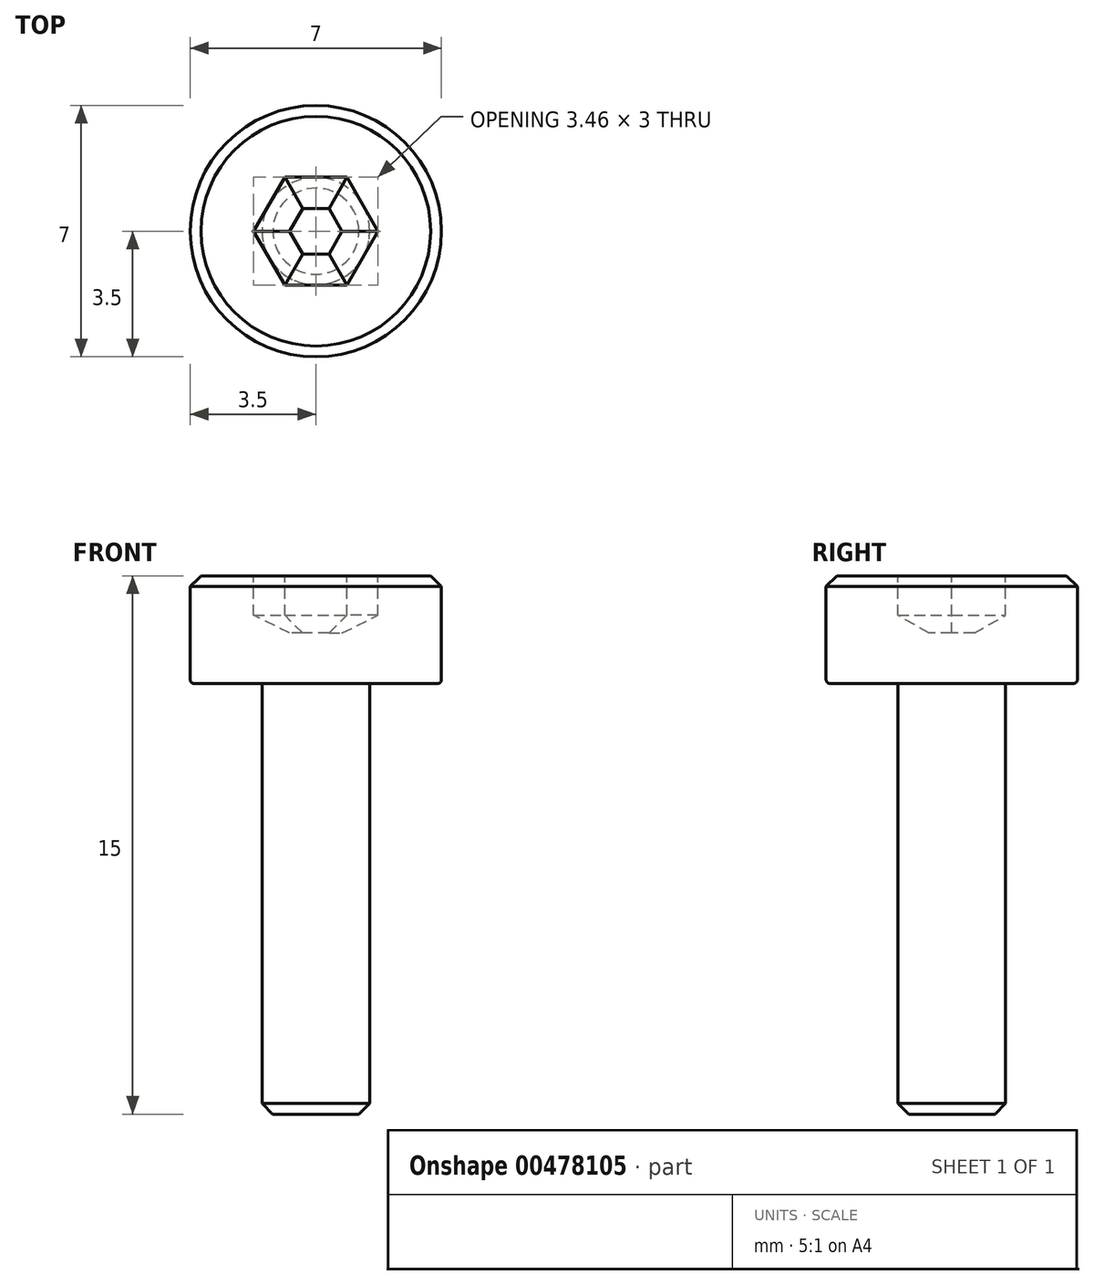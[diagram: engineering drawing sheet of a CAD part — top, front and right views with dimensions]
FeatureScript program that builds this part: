
annotation { "Feature Type Name" : "Feature", "Feature Type Description" : "" }
export const myFeature = defineFeature(function(context is Context, id is Id, definition is map)
    precondition{}
    {
        {
            var Q0;
            Q0=qCreatedBy(makeId("Front.planeOp"),FACE);
            var sketch = newSketch(context, id + "F0", { "sketchPlane" : qUnion([Q0])});
            skLineSegment(sketch, "E0", {"start": v(0, 0) * mm, "end": v(0, -13.37) * mm, "construction": true});
            skLineSegment(sketch, "E1", {"start": v(0, 0) * mm, "end": v(3.5, 0) * mm});
            skLineSegment(sketch, "E2", {"start": v(3.5, 0) * mm, "end": v(3.5, -3) * mm});
            skLineSegment(sketch, "E3", {"start": v(3.5, -3) * mm, "end": v(1.5, -3) * mm});
            skLineSegment(sketch, "E4", {"start": v(1.5, -3) * mm, "end": v(1.5, -15) * mm});
            skLineSegment(sketch, "E5", {"start": v(1.5, -15) * mm, "end": v(0, -15) * mm});
            skLineSegment(sketch, "E6", {"start": v(0, -15) * mm, "end": v(0, 0) * mm});
            skSolve(sketch);
        }
        {
            var Q0;
            Q0=qSketchRegion(id+"F0",true);
            var Q1;
            Q1=sQuery(id+"F0.wireOp",EDGE,"E6");
            revolve(context, id + "F1", {"entities" : qUnion([Q0]), "axis" : qUnion([Q1]), "revolveType" : RevolveType.FULL});
        }
        {
            var Q0;
            Q0=makeQuery(id+"F1.opRevolve","SWEPT_FACE",FACE,{"disambiguationData":[OSD([sQuery(id+"F0.wireOp",EDGE,"E1")])]});
            var sketch = newSketch(context, id + "F2", { "sketchPlane" : qUnion([Q0])});
            skCircle(sketch, "E7.cCircle", {"center": v(0, 0) * mm, "radius": 1.5 * mm, "construction": true});
            skLineSegment(sketch, "E7.0", {"start": v(-0.87, 1.5) * mm, "end": v(0.87, 1.5) * mm});
            skLineSegment(sketch, "E7.1", {"start": v(0.87, 1.5) * mm, "end": v(1.73, 0) * mm});
            skLineSegment(sketch, "E7.2", {"start": v(1.73, 0) * mm, "end": v(0.87, -1.5) * mm});
            skLineSegment(sketch, "E7.3", {"start": v(0.87, -1.5) * mm, "end": v(-0.87, -1.5) * mm});
            skLineSegment(sketch, "E7.4", {"start": v(-0.87, -1.5) * mm, "end": v(-1.73, 0) * mm});
            skLineSegment(sketch, "E7.5", {"start": v(-1.73, 0) * mm, "end": v(-0.87, 1.5) * mm});
            skPoint(sketch, "E7.0.midPoint", {"position": v(0, 1.5) * mm});
            skSolve(sketch);
        }
        {
            var Q0;
            Q0=makeQuery(id+"F2.imprint","IMPRINT",FACE,{"disambiguationData":[TD([[makeQuery(id+"F2.imprint","IMPRINT",EDGE,{"derivedFrom":sQuery(id+"F2.wireOp",EDGE,"E7.0")}),-1.0]])]});
            extrude(context, id + "F3", {"entities" : qUnion([Q0]), "operationType" : NewBodyOperationType.REMOVE, "oppositeDirection" : true, "depth" : 1.6 * mm});
        }
        {
            var Q0;
            Q0=makeQuery(id+"F3.boolean.opBoolean","COPY",FACE,{"derivedFrom":makeQuery(id+"F3.opExtrude","CAP_FACE",FACE,{"disambiguationData":[OSD([sQuery(id+"F2.wireOp",EDGE,"E7.0"),sQuery(id+"F2.wireOp",EDGE,"E7.1"),sQuery(id+"F2.wireOp",EDGE,"E7.2"),sQuery(id+"F2.wireOp",EDGE,"E7.3"),sQuery(id+"F2.wireOp",EDGE,"E7.4"),sQuery(id+"F2.wireOp",EDGE,"E7.5")])],"isStart":false})});
            chamfer(context, id + "F4", {"entities" : qUnion([Q0]), "chamferType" : ChamferType.OFFSET_ANGLE, "width" : .5 * mm, "oppositeDirection" : false, "angle" : 60 * degree, "tangentPropagation" : true});
        }
        {
            var Q0;
            Q0=makeQuery(id+"F1.opRevolve","SWEPT_EDGE",EDGE,{"disambiguationData":[OSD([sQuery(id+"F0.wireOp",EDGE,"E1"),sQuery(id+"F0.wireOp",EDGE,"E2")])]});
            var Q1;
            Q1=makeQuery(id+"F1.opRevolve","SWEPT_EDGE",EDGE,{"disambiguationData":[OSD([sQuery(id+"F0.wireOp",EDGE,"E4"),sQuery(id+"F0.wireOp",EDGE,"E5")])]});
            chamfer(context, id + "F5", {"entities" : qUnion([Q0, Q1]), "width" : .3 * mm, "tangentPropagation" : true});
        }
        {
            var Q0;
            Q0=makeQuery(id+"F1.opRevolve","SWEPT_EDGE",EDGE,{"disambiguationData":[OSD([sQuery(id+"F0.wireOp",EDGE,"E2"),sQuery(id+"F0.wireOp",EDGE,"E3")])]});
            fillet(context, id + "F6", {"entities" : qUnion([Q0]), "radius" : .1 * mm, "tangentPropagation" : true, "allowEdgeOverflow" : false});
        }
        {
            var Q0;
            Q0=makeQuery(id+"F1.opRevolve","SWEPT_BODY",BODY,{"disambiguationData":[OSD([sQuery(id+"F0.wireOp",EDGE,"E1"),sQuery(id+"F0.wireOp",EDGE,"E2"),sQuery(id+"F0.wireOp",EDGE,"E3"),sQuery(id+"F0.wireOp",EDGE,"E4"),sQuery(id+"F0.wireOp",EDGE,"E5"),sQuery(id+"F0.wireOp",EDGE,"E6")])]});
            transform(context, id + "F7", {"entities" : qUnion([Q0]), "transformType" : TransformType.COPY});
        }
    });
